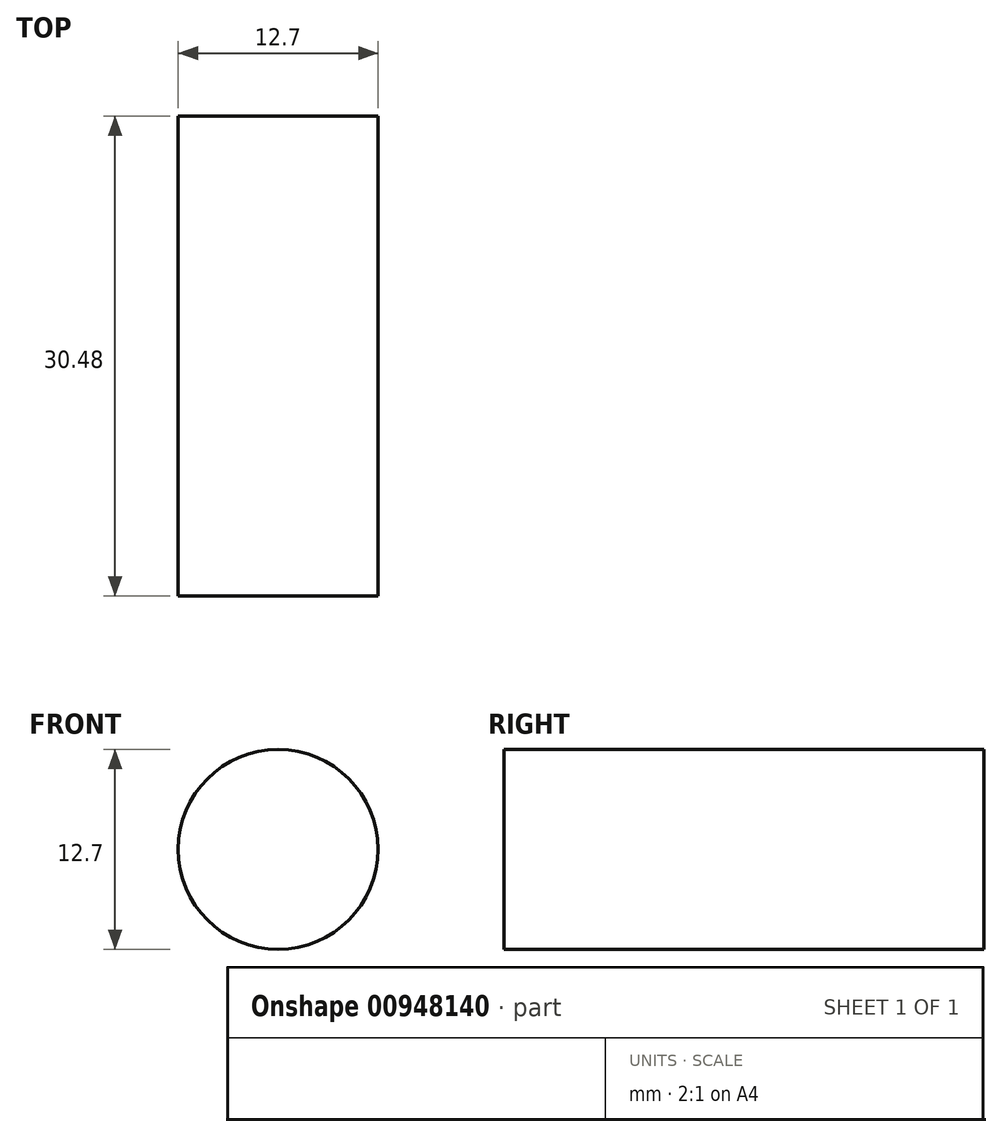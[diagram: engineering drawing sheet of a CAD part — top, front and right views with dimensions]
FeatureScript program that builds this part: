
annotation { "Feature Type Name" : "Feature", "Feature Type Description" : "" }
export const myFeature = defineFeature(function(context is Context, id is Id, definition is map)
    precondition{}
    {
        {
            var Q0;
            Q0=qCreatedBy(makeId("Front.planeOp"),FACE);
            var sketch = newSketch(context, id + "F0", { "sketchPlane" : qUnion([Q0])});
            skCircle(sketch, "E0", {"center": v(-23.3, 14.44) * mm, "radius": 6.35 * mm});
            skSolve(sketch);
        }
        {
            var Q0;
            Q0=makeQuery(id+"F0.imprint","IMPRINT",FACE,{"disambiguationData":[TD([[makeQuery(id+"F0.imprint","IMPRINT",EDGE,{"derivedFrom":sQuery(id+"F0.wireOp",EDGE,"E0")}),1.0]])]});
            extrude(context, id + "F1", {"entities" : qUnion([Q0]), "depth" : 30.48 * mm, "offsetDistance" : 25.4 * mm});
        }
    });
